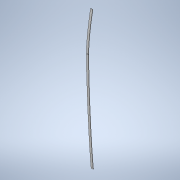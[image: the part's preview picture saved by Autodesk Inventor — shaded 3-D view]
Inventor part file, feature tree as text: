
AUTODESK INVENTOR PART (.ipt)
format: ipt  version: 2020.3 (Build 243373010, 373A)  size: 189,952 bytes
history: native  units: mm
features: other x31, plane x1, extrude x1
ambient origin geometry x8: Origin, YZ Plane, XZ Plane, XY Plane, X Axis, Y Axis, Z Axis, Center Point
bodies: Body1 (feature_tree)
feature tree (33):
  other  "base_sketch.ipt"
  plane  "Work Plane1"
  extrude  "Extrusion1"  Depth=10.0mm
  other  "stringer"
  other  "stringer_inside"
  other  "bulkhead_main"
  other  "bulkhead_F1"
  other  "bulkhead_front"
  other  "bulkhead_B1"
  other  "bulkhead_B2"
  other  "transom"
  other  "stinger_bottom_liner"
  other  "bulkhead_front_tunnel_top"
  other  "bulkhead_front_tunnel_bottom"
  other  "bulkhead_main_top"
  other  "bulkhead_main_tunnel_bottom"
  other  "bulkhead_main_tunnel_standoff"
  other  "bulkhead_front_top"
  other  "bulkhead_front_bottom"
  other  "bulkhead_F1_tunnel_bottom"
  other  "bulkhead_F1_tunnel_top"
  other  "bulkhead_F1_top"
  other  "bulkhead_F1_tunnel_standoff"
  other  "bulkhead_F1_bottom"
  other  "bulkhead_F2_bottom"
  other  "bulkhead_F2_top"
  other  "bulkhead_B1_bottom"
  other  "bulkhead_B1_top"
  other  "bulkhead_B1_tunnel_standoff"
  other  "bulkhead_B1_tunnel_bottom"
  other  "bulkhead_B2_top"
  other  "bulkhead_B2_tunnel_bottom"
  other  "bulkhead_B2_bottom"
